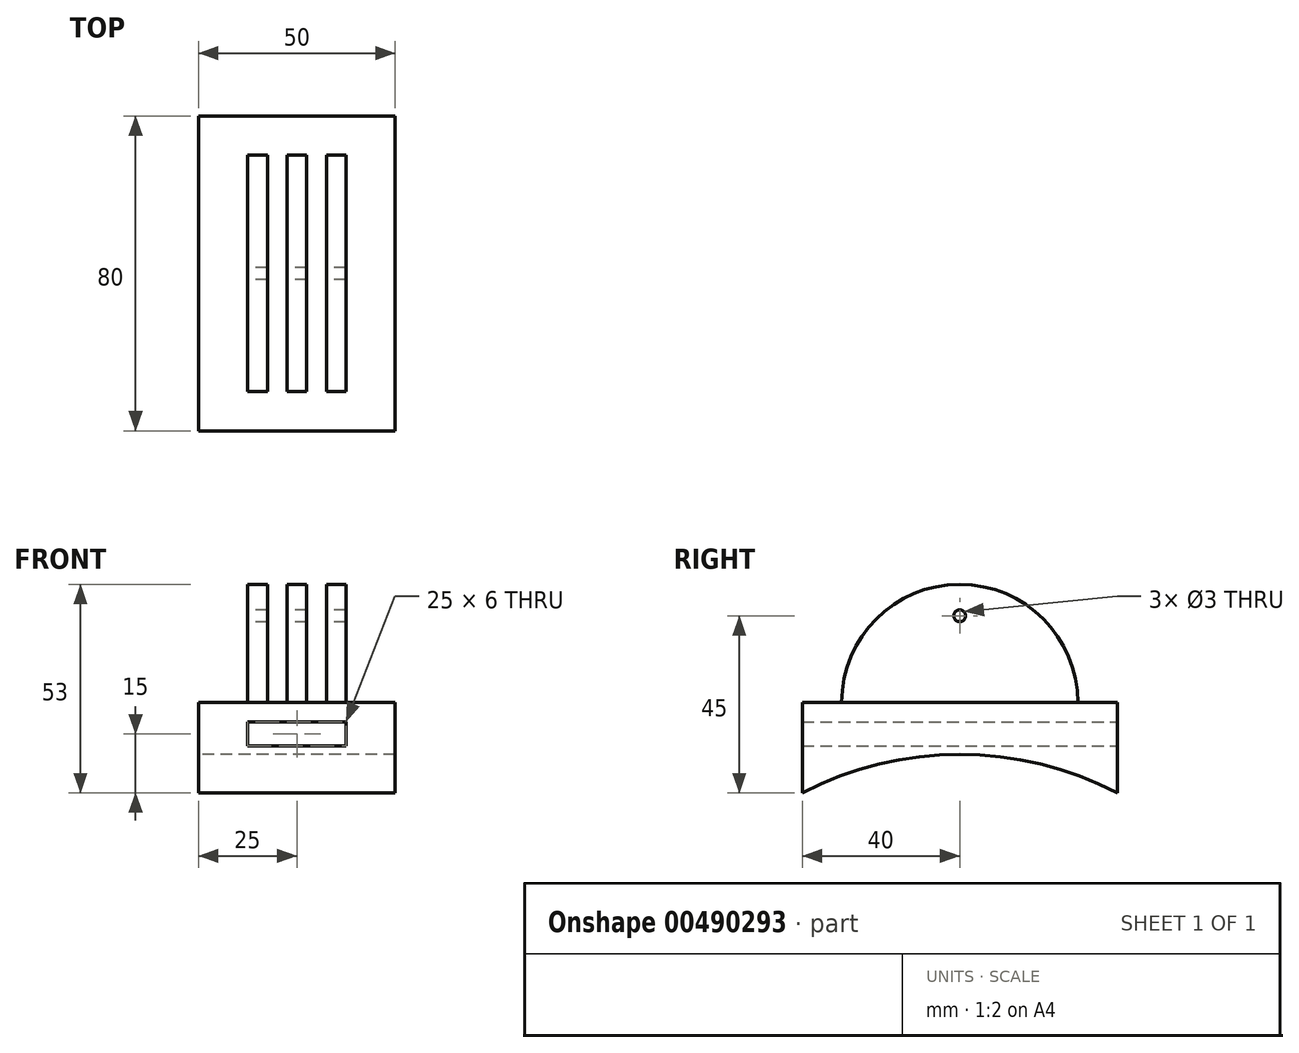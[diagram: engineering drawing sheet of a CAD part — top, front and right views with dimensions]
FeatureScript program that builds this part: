
annotation { "Feature Type Name" : "Feature", "Feature Type Description" : "" }
export const myFeature = defineFeature(function(context is Context, id is Id, definition is map)
    precondition{}
    {
        {
            var Q0;
            Q0=qCreatedBy(makeId("Top.planeOp"),FACE);
            var sketch = newSketch(context, id + "F0", { "sketchPlane" : qUnion([Q0])});
            skLineSegment(sketch, "E0.bottom", {"start": v(-25, 40) * mm, "end": v(25, 40) * mm});
            skLineSegment(sketch, "E0.top", {"start": v(-25, -40) * mm, "end": v(25, -40) * mm});
            skLineSegment(sketch, "E0.left", {"start": v(-25, 40) * mm, "end": v(-25, -40) * mm});
            skLineSegment(sketch, "E0.right", {"start": v(25, 40) * mm, "end": v(25, -40) * mm});
            skPoint(sketch, "E0.middle", {"position": v(0, 0) * mm});
            skSolve(sketch);
        }
        {
            var Q0;
            Q0=makeQuery(id+"F0.imprint","IMPRINT",FACE,{"disambiguationData":[TD([[makeQuery(id+"F0.imprint","IMPRINT",EDGE,{"derivedFrom":sQuery(id+"F0.wireOp",EDGE,"E0.bottom")}),-1.0]])]});
            extrude(context, id + "F1", {"entities" : qUnion([Q0]), "depth" : 6 * mm, "offsetDistance" : 25 * mm});
        }
        {
            var Q0;
            Q0=makeQuery(id+"F1.opExtrude","CAP_FACE",FACE,{"disambiguationData":[OSD([sQuery(id+"F0.wireOp",EDGE,"E0.bottom"),sQuery(id+"F0.wireOp",EDGE,"E0.top"),sQuery(id+"F0.wireOp",EDGE,"E0.left"),sQuery(id+"F0.wireOp",EDGE,"E0.right")])],"isStart":false});
            var sketch = newSketch(context, id + "F2", { "sketchPlane" : qUnion([Q0])});
            skLineSegment(sketch, "E1", {"start": v(0, 40) * mm, "end": v(0, -40) * mm, "construction": true});
            skLineSegment(sketch, "E2.bottom", {"start": v(-2.5, 30) * mm, "end": v(2.5, 30) * mm});
            skLineSegment(sketch, "E2.top", {"start": v(-2.5, -30) * mm, "end": v(2.5, -30) * mm});
            skLineSegment(sketch, "E2.left", {"start": v(-2.5, 30) * mm, "end": v(-2.5, -30) * mm});
            skLineSegment(sketch, "E2.right", {"start": v(2.5, 30) * mm, "end": v(2.5, -30) * mm});
            skPoint(sketch, "E2.middle", {"position": v(0, 0) * mm});
            skLineSegment(sketch, "E3.1.0.0", {"start": v(7.5, 30) * mm, "end": v(12.5, 30) * mm});
            skLineSegment(sketch, "E3.1.0.1", {"start": v(7.5, 30) * mm, "end": v(7.5, -30) * mm});
            skLineSegment(sketch, "E3.1.0.2", {"start": v(7.5, -30) * mm, "end": v(12.5, -30) * mm});
            skLineSegment(sketch, "E3.1.0.3", {"start": v(12.5, 30) * mm, "end": v(12.5, -30) * mm});
            skPoint(sketch, "E3.1.0.4", {"position": v(10, 0) * mm});
            skLineSegment(sketch, "E3.direction1", {"start": v(-2.5, -30) * mm, "end": v(7.5, -30) * mm, "construction": true});
            skLineSegment(sketch, "E4.1.0.0", {"start": v(-12.5, 30) * mm, "end": v(-7.5, 30) * mm});
            skLineSegment(sketch, "E4.1.0.1", {"start": v(-12.5, -30) * mm, "end": v(-7.5, -30) * mm});
            skLineSegment(sketch, "E4.1.0.2", {"start": v(-12.5, 30) * mm, "end": v(-12.5, -30) * mm});
            skPoint(sketch, "E4.1.0.3", {"position": v(-10, 0) * mm});
            skLineSegment(sketch, "E4.1.0.4", {"start": v(-7.5, 30) * mm, "end": v(-7.5, -30) * mm});
            skLineSegment(sketch, "E4.direction1", {"start": v(-2.5, -30) * mm, "end": v(-12.5, -30) * mm, "construction": true});
            skSolve(sketch);
        }
        {
            var Q0;
            Q0=makeQuery(id+"F2.imprint","IMPRINT",FACE,{"disambiguationData":[TD([[makeQuery(id+"F2.imprint","IMPRINT",EDGE,{"derivedFrom":sQuery(id+"F2.wireOp",EDGE,"E2.bottom")}),-1.0]])]});
            var Q1;
            Q1=makeQuery(id+"F2.imprint","IMPRINT",FACE,{"disambiguationData":[TD([[makeQuery(id+"F2.imprint","IMPRINT",EDGE,{"derivedFrom":sQuery(id+"F2.wireOp",EDGE,"E4.1.0.0")}),-1.0]])]});
            var Q2;
            Q2=makeQuery(id+"F2.imprint","IMPRINT",FACE,{"disambiguationData":[TD([[makeQuery(id+"F2.imprint","IMPRINT",EDGE,{"derivedFrom":sQuery(id+"F2.wireOp",EDGE,"E3.1.0.0")}),-1.0]])]});
            extrude(context, id + "F3", {"entities" : qUnion([Q0, Q1, Q2]), "operationType" : NewBodyOperationType.ADD, "depth" : 30 * mm, "offsetDistance" : 25 * mm});
        }
        {
            var Q0;
            Q0=makeQuery(id+"F3.opExtrude","CAP_EDGE",EDGE,{"disambiguationData":[OSD([sQuery(id+"F2.wireOp",EDGE,"E3.1.0.0")])],"isStart":false});
            var Q1;
            Q1=makeQuery(id+"F3.opExtrude","CAP_EDGE",EDGE,{"disambiguationData":[OSD([sQuery(id+"F2.wireOp",EDGE,"E2.bottom")])],"isStart":false});
            var Q2;
            Q2=makeQuery(id+"F3.opExtrude","CAP_EDGE",EDGE,{"disambiguationData":[OSD([sQuery(id+"F2.wireOp",EDGE,"E4.1.0.0")])],"isStart":false});
            var Q3;
            Q3=makeQuery(id+"F3.opExtrude","CAP_EDGE",EDGE,{"disambiguationData":[OSD([sQuery(id+"F2.wireOp",EDGE,"E4.1.0.1")])],"isStart":false});
            var Q4;
            Q4=makeQuery(id+"F3.opExtrude","CAP_EDGE",EDGE,{"disambiguationData":[OSD([sQuery(id+"F2.wireOp",EDGE,"E2.top")])],"isStart":false});
            var Q5;
            Q5=makeQuery(id+"F3.opExtrude","CAP_EDGE",EDGE,{"disambiguationData":[OSD([sQuery(id+"F2.wireOp",EDGE,"E3.1.0.2")])],"isStart":false});
            fillet(context, id + "F4", {"entities" : qUnion([Q0, Q1, Q2, Q3, Q4, Q5]), "tangentPropagation" : true, "radius" : 30 * mm, "defaultsChanged" : true, "vertexSettings" : [], "allowEdgeOverflow" : false});
        }
        {
            var Q0;
            Q0=makeQuery(id+"F1.opExtrude","CAP_FACE",FACE,{"disambiguationData":[OSD([sQuery(id+"F0.wireOp",EDGE,"E0.bottom"),sQuery(id+"F0.wireOp",EDGE,"E0.top"),sQuery(id+"F0.wireOp",EDGE,"E0.left"),sQuery(id+"F0.wireOp",EDGE,"E0.right")])],"isStart":true});
            extrude(context, id + "F5", {"entities" : qUnion([Q0]), "operationType" : NewBodyOperationType.ADD, "depth" : 40 * mm, "offsetDistance" : 25 * mm});
        }
        {
            var Q0;
            {var subQ0=sQuery(id+"F0.wireOp",EDGE,"E0.left");Q0=makeQuery(id+"F5.boolean.opBoolean","MERGE",FACE,{"derivedFrom":[makeQuery(id+"F1.opExtrude","SWEPT_FACE",FACE,{"disambiguationData":[OSD([subQ0])]}),makeQuery(id+"F5.opExtrude","SWEPT_FACE",FACE,{"disambiguationData":[OSD([subQ0])]})]});}
            var sketch = newSketch(context, id + "F6", { "sketchPlane" : qUnion([Q0])});
            skArc(sketch, "E5", {"start": v(40, -17) * mm, "mid": v(0, -7.21) * mm, "end": v(-40, -17) * mm});
            skSolve(sketch);
        }
        {
            var Q0;
            Q0 = qSketchRegion(id + "F6", true);
            var Q1;
            {var subQ0=sQuery(id+"F6.wireOp",EDGE,"E5");Q1=makeQuery(id+"F6.imprint","IMPRINT",FACE,{"disambiguationData":[TD([[makeQuery(id+"F6.imprint","IMPRINT",EDGE,{"derivedFrom":subQ0}),1.0]])]});}
            extrude(context, id + "F7", {"entities" : qUnion([Q0, Q1]), "operationType" : NewBodyOperationType.REMOVE, "oppositeDirection" : true, "depth" : 65 * mm, "offsetDistance" : 25 * mm});
        }
        {
            var Q0;
            {var subQ0=sQuery(id+"F0.wireOp",EDGE,"E0.bottom");Q0=makeQuery(id+"F5.boolean.opBoolean","MERGE",FACE,{"derivedFrom":[makeQuery(id+"F1.opExtrude","SWEPT_FACE",FACE,{"disambiguationData":[OSD([subQ0])]}),makeQuery(id+"F5.opExtrude","SWEPT_FACE",FACE,{"disambiguationData":[OSD([subQ0])]})]});}
            var sketch = newSketch(context, id + "F8", { "sketchPlane" : qUnion([Q0])});
            skLineSegment(sketch, "E6.bottom", {"start": v(12.5, -5) * mm, "end": v(-12.5, -5) * mm});
            skLineSegment(sketch, "E6.top", {"start": v(12.5, 1) * mm, "end": v(-12.5, 1) * mm});
            skLineSegment(sketch, "E6.left", {"start": v(12.5, -5) * mm, "end": v(12.5, 1) * mm});
            skLineSegment(sketch, "E6.right", {"start": v(-12.5, -5) * mm, "end": v(-12.5, 1) * mm});
            skPoint(sketch, "E6.middle", {"position": v(0, -2) * mm});
            skSolve(sketch);
        }
        {
            var Q0;
            Q0 = qSketchRegion(id + "F8", true);
            extrude(context, id + "F9", {"entities" : qUnion([Q0]), "operationType" : NewBodyOperationType.REMOVE, "oppositeDirection" : true, "depth" : 115.9 * mm, "offsetDistance" : 25 * mm});
        }
        {
            var Q0;
            Q0=makeQuery(id+"F3.opExtrude","SWEPT_FACE",FACE,{"disambiguationData":[OSD([sQuery(id+"F2.wireOp",EDGE,"E4.1.0.2")])]});
            var sketch = newSketch(context, id + "F10", { "sketchPlane" : qUnion([Q0])});
            skCircle(sketch, "E7", {"center": v(0, 28) * mm, "radius": 1.5 * mm});
            skSolve(sketch);
        }
        {
            var Q0;
            Q0 = qSketchRegion(id + "F10", true);
            extrude(context, id + "F11", {"entities" : qUnion([Q0]), "operationType" : NewBodyOperationType.REMOVE, "oppositeDirection" : true, "depth" : 30.7 * mm, "offsetDistance" : 25 * mm});
        }
    });
